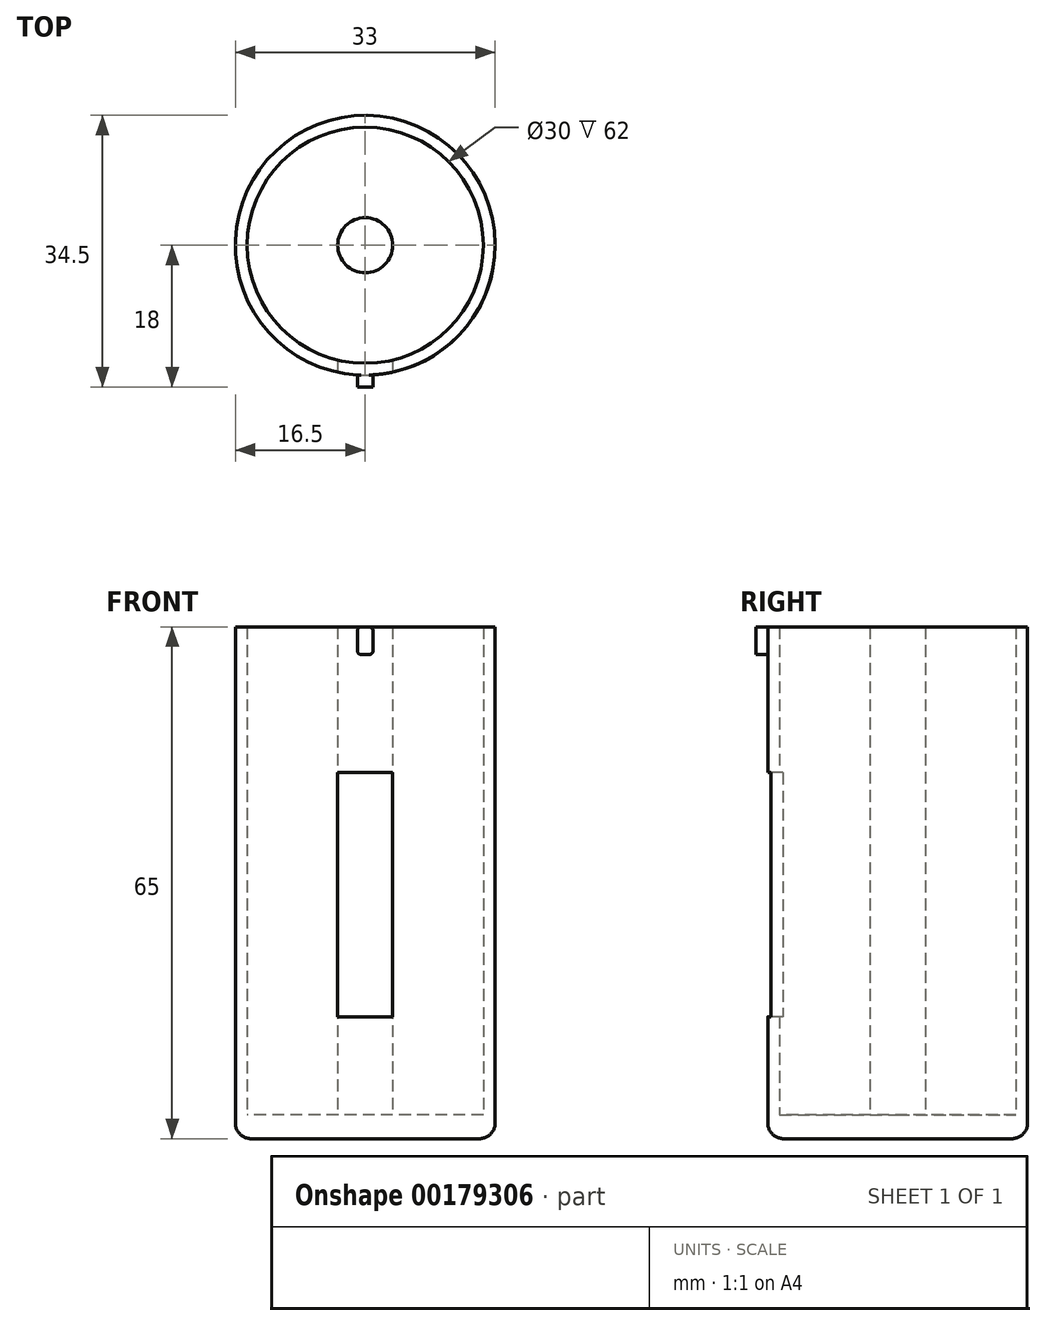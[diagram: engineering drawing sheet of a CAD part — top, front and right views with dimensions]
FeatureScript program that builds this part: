
annotation { "Feature Type Name" : "Feature", "Feature Type Description" : "" }
export const myFeature = defineFeature(function(context is Context, id is Id, definition is map)
    precondition{}
    {
        {
            var Q0;
            Q0=qCreatedBy(makeId("Top.planeOp"),FACE);
            var sketch = newSketch(context, id + "F0", { "sketchPlane" : qUnion([Q0])});
            skCircle(sketch, "E0", {"center": v(0, 0) * mm, "radius": 15 * mm});
            skCircle(sketch, "E1", {"center": v(0, 0) * mm, "radius": 16.5 * mm});
            skSolve(sketch);
        }
        {
            var Q0;
            Q0=makeQuery(id+"F0.imprint","IMPRINT",FACE,{"disambiguationData":[TD([[makeQuery(id+"F0.imprint","IMPRINT",EDGE,{"derivedFrom":sQuery(id+"F0.wireOp",EDGE,"E0")}),-1.0]])]});
            var Q1;
            Q1=makeQuery(id+"F0.imprint","IMPRINT",FACE,{"disambiguationData":[TD([[makeQuery(id+"F0.imprint","IMPRINT",EDGE,{"derivedFrom":sQuery(id+"F0.wireOp",EDGE,"E0")}),1.0]])]});
            extrude(context, id + "F1", {"entities" : qUnion([Q0, Q1]), "depth" : 3 * mm});
        }
        {
            var Q0;
            Q0=makeQuery(id+"F1.opExtrude","CAP_FACE",FACE,{"disambiguationData":[OSD([sQuery(id+"F0.wireOp",EDGE,"E1")])],"isStart":false});
            var sketch = newSketch(context, id + "F2", { "sketchPlane" : qUnion([Q0])});
            skCircle(sketch, "E2", {"center": v(0, 0) * mm, "radius": 15 * mm});
            skSolve(sketch);
        }
        {
            var Q0;
            Q0=makeQuery(id+"F2.imprint","IMPRINT",FACE,{"disambiguationData":[TD([[makeQuery(id+"F2.imprint","IMPRINT",EDGE,{"derivedFrom":sQuery(id+"F2.wireOp",EDGE,"E2")}),-1.0]])]});
            extrude(context, id + "F3", {"entities" : qUnion([Q0]), "operationType" : NewBodyOperationType.ADD, "depth" : 62 * mm});
        }
        {
            var Q0;
            Q0=makeQuery(id+"F1.opExtrude","CAP_FACE",FACE,{"disambiguationData":[OSD([sQuery(id+"F0.wireOp",EDGE,"E1")])],"isStart":false});
            var sketch = newSketch(context, id + "F4", { "sketchPlane" : qUnion([Q0])});
            skCircle(sketch, "E3", {"center": v(0, 0) * mm, "radius": 3.5 * mm});
            skSolve(sketch);
        }
        {
            var Q0;
            Q0=makeQuery(id+"F4.imprint","IMPRINT",FACE,{"disambiguationData":[TD([[makeQuery(id+"F4.imprint","IMPRINT",EDGE,{"derivedFrom":sQuery(id+"F4.wireOp",EDGE,"E3")}),1.0]])]});
            extrude(context, id + "F5", {"entities" : qUnion([Q0]), "operationType" : NewBodyOperationType.ADD, "depth" : 62 * mm});
        }
        {
            var Q0;
            Q0=qCreatedBy(makeId("Front.planeOp"),FACE);
            cPlane(context, id + "F6", {"entities" : qUnion([Q0]), "cplaneType" : CPlaneType.OFFSET, "offset" : 30 * mm, "width" : 150 * mm, "height" : 150 * mm});
        }
        {
            var Q0;
            Q0=qCreatedBy(id+"F6.planeOp",FACE);
            var sketch = newSketch(context, id + "F7", { "sketchPlane" : qUnion([Q0])});
            skLineSegment(sketch, "E4.bottom", {"start": v(3.5, 46.5) * mm, "end": v(-3.5, 46.5) * mm});
            skLineSegment(sketch, "E4.top", {"start": v(3.5, 15.5) * mm, "end": v(-3.5, 15.5) * mm});
            skLineSegment(sketch, "E4.left", {"start": v(3.5, 46.5) * mm, "end": v(3.5, 15.5) * mm});
            skLineSegment(sketch, "E4.right", {"start": v(-3.5, 46.5) * mm, "end": v(-3.5, 15.5) * mm});
            skPoint(sketch, "E4.middle", {"position": v(0, 31) * mm});
            skSolve(sketch);
        }
        {
            var Q0;
            Q0 = qSketchRegion(id + "F7", true);
            extrude(context, id + "F8", {"entities" : qUnion([Q0]), "operationType" : NewBodyOperationType.REMOVE, "oppositeDirection" : true, "depth" : 20 * mm});
        }
        {
            var Q0;
            Q0=qCreatedBy(makeId("Front.planeOp"),FACE);
            cPlane(context, id + "F9", {"entities" : qUnion([Q0]), "cplaneType" : CPlaneType.OFFSET, "offset" : 16.5 * mm, "width" : 150 * mm, "height" : 150 * mm});
        }
        {
            var Q0;
            Q0=qCreatedBy(id+"F9.planeOp",FACE);
            var sketch = newSketch(context, id + "F10", { "sketchPlane" : qUnion([Q0])});
            skLineSegment(sketch, "E5", {"start": v(0, 65) * mm, "end": v(-0.5, 65) * mm});
            skLineSegment(sketch, "E6", {"start": v(-1, 64.5) * mm, "end": v(-1, 62) * mm});
            skLineSegment(sketch, "E7", {"start": v(-0.5, 61.5) * mm, "end": v(0.5, 61.5) * mm});
            skLineSegment(sketch, "E8", {"start": v(1, 62) * mm, "end": v(1, 64.5) * mm});
            skLineSegment(sketch, "E9", {"start": v(0.5, 65) * mm, "end": v(0, 65) * mm});
            skPoint(sketch, "E10.visualSharp", {"position": v(-1, 65) * mm});
            skArc(sketch, "E10.filletArc", {"start": v(-0.5, 65) * mm, "mid": v(-0.85, 64.85) * mm, "end": v(-1, 64.5) * mm});
            skPoint(sketch, "E11.visualSharp", {"position": v(1, 65) * mm});
            skArc(sketch, "E11.filletArc", {"start": v(1, 64.5) * mm, "mid": v(0.85, 64.85) * mm, "end": v(0.5, 65) * mm});
            skPoint(sketch, "E12.visualSharp", {"position": v(-1, 61.5) * mm});
            skArc(sketch, "E12.filletArc", {"start": v(-1, 62) * mm, "mid": v(-0.85, 61.65) * mm, "end": v(-0.5, 61.5) * mm});
            skPoint(sketch, "E13.visualSharp", {"position": v(1, 61.5) * mm});
            skArc(sketch, "E13.filletArc", {"start": v(0.5, 61.5) * mm, "mid": v(0.85, 61.65) * mm, "end": v(1, 62) * mm});
            skSolve(sketch);
        }
        {
            var Q0;
            Q0 = qSketchRegion(id + "F10", true);
            extrude(context, id + "F11", {"entities" : qUnion([Q0]), "operationType" : NewBodyOperationType.ADD, "endBound" : BoundingType.SYMMETRIC, "depth" : 3 * mm});
        }
        {
            var Q0;
            Q0=makeQuery(id+"F1.opExtrude","CAP_EDGE",EDGE,{"disambiguationData":[OSD([sQuery(id+"F0.wireOp",EDGE,"E1")])],"isStart":true});
            fillet(context, id + "F12", {"entities" : qUnion([Q0]), "radius" : 2 * mm, "tangentPropagation" : true, "allowEdgeOverflow" : false});
        }
    });
